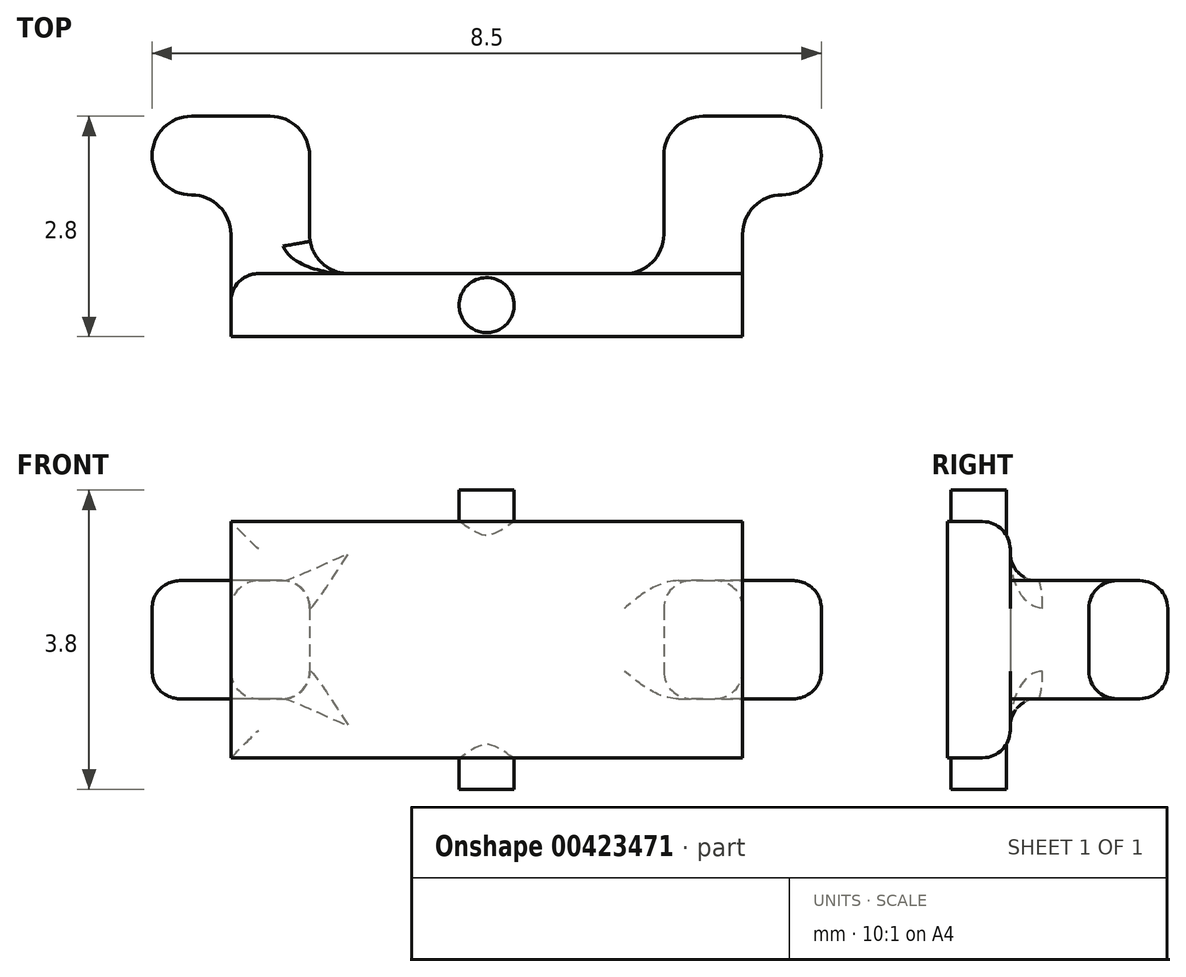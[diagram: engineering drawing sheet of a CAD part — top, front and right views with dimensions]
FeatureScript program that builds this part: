
annotation { "Feature Type Name" : "Feature", "Feature Type Description" : "" }
export const myFeature = defineFeature(function(context is Context, id is Id, definition is map)
    precondition{}
    {
        {
            var Q0;
            Q0=qCreatedBy(makeId("Top.planeOp"),FACE);
            var sketch = newSketch(context, id + "F0", { "sketchPlane" : qUnion([Q0])});
            skLineSegment(sketch, "E0", {"start": v(-3.25, 0) * mm, "end": v(3.25, 0) * mm});
            skPoint(sketch, "E1", {"position": v(0, 0) * mm});
            skLineSegment(sketch, "E2", {"start": v(0, -1.15) * mm, "end": v(0, 7.11) * mm, "construction": true});
            skLineSegment(sketch, "E3", {"start": v(2.25, 1.3) * mm, "end": v(2.25, 2.3) * mm});
            skLineSegment(sketch, "E4", {"start": v(-2.25, 1.3) * mm, "end": v(-2.25, 2.3) * mm});
            skLineSegment(sketch, "E5", {"start": v(-1.75, 0.8) * mm, "end": v(1.75, 0.8) * mm});
            skPoint(sketch, "E6", {"position": v(0, 0.8) * mm});
            skLineSegment(sketch, "E7", {"start": v(-2.75, 2.8) * mm, "end": v(-3.75, 2.8) * mm});
            skLineSegment(sketch, "E8", {"start": v(2.75, 2.8) * mm, "end": v(3.75, 2.8) * mm});
            skLineSegment(sketch, "E9", {"start": v(-4.25, 2.3) * mm, "end": v(-4.25, 2.3) * mm});
            skLineSegment(sketch, "E10", {"start": v(-3.75, 1.8) * mm, "end": v(-3.75, 1.8) * mm});
            skLineSegment(sketch, "E11", {"start": v(-3.25, 1.3) * mm, "end": v(-3.25, 1.3) * mm});
            skLineSegment(sketch, "E12", {"start": v(4.25, 2.3) * mm, "end": v(4.25, 2.3) * mm});
            skLineSegment(sketch, "E13", {"start": v(3.75, 1.8) * mm, "end": v(3.75, 1.8) * mm});
            skLineSegment(sketch, "E14", {"start": v(3.25, 1.3) * mm, "end": v(3.25, 1.3) * mm});
            skPoint(sketch, "E15.visualSharp", {"position": v(-2.25, 0.8) * mm});
            skArc(sketch, "E15.filletArc", {"start": v(-2.25, 1.3) * mm, "mid": v(-2.1, 0.95) * mm, "end": v(-1.75, 0.8) * mm});
            skPoint(sketch, "E16.visualSharp", {"position": v(2.25, 0.8) * mm});
            skArc(sketch, "E16.filletArc", {"start": v(1.75, 0.8) * mm, "mid": v(2.1, 0.95) * mm, "end": v(2.25, 1.3) * mm});
            skPoint(sketch, "E17.visualSharp", {"position": v(3.25, 1.8) * mm});
            skArc(sketch, "E17.filletArc", {"start": v(3.75, 1.8) * mm, "mid": v(3.4, 1.65) * mm, "end": v(3.25, 1.3) * mm});
            skPoint(sketch, "E18.visualSharp", {"position": v(-3.25, 1.8) * mm});
            skArc(sketch, "E18.filletArc", {"start": v(-3.25, 1.3) * mm, "mid": v(-3.4, 1.65) * mm, "end": v(-3.75, 1.8) * mm});
            skPoint(sketch, "E19.visualSharp", {"position": v(-2.25, 2.8) * mm});
            skArc(sketch, "E19.filletArc", {"start": v(-2.25, 2.3) * mm, "mid": v(-2.4, 2.65) * mm, "end": v(-2.75, 2.8) * mm});
            skPoint(sketch, "E20.visualSharp", {"position": v(2.25, 2.8) * mm});
            skArc(sketch, "E20.filletArc", {"start": v(2.75, 2.8) * mm, "mid": v(2.4, 2.65) * mm, "end": v(2.25, 2.3) * mm});
            skPoint(sketch, "E21.visualSharp", {"position": v(4.25, 2.8) * mm});
            skArc(sketch, "E21.filletArc", {"start": v(4.25, 2.3) * mm, "mid": v(4.1, 2.65) * mm, "end": v(3.75, 2.8) * mm});
            skPoint(sketch, "E22.visualSharp", {"position": v(4.25, 1.8) * mm});
            skArc(sketch, "E22.filletArc", {"start": v(3.75, 1.8) * mm, "mid": v(4.1, 1.95) * mm, "end": v(4.25, 2.3) * mm});
            skPoint(sketch, "E23.visualSharp", {"position": v(-4.25, 2.8) * mm});
            skArc(sketch, "E23.filletArc", {"start": v(-3.75, 2.8) * mm, "mid": v(-4.1, 2.65) * mm, "end": v(-4.25, 2.3) * mm});
            skPoint(sketch, "E24.visualSharp", {"position": v(-4.25, 1.8) * mm});
            skArc(sketch, "E24.filletArc", {"start": v(-4.25, 2.3) * mm, "mid": v(-4.1, 1.95) * mm, "end": v(-3.75, 1.8) * mm});
            skLineSegment(sketch, "E25", {"start": v(-3.25, 1.3) * mm, "end": v(-3.25, 0) * mm});
            skLineSegment(sketch, "E26", {"start": v(3.25, 1.3) * mm, "end": v(3.25, 0) * mm});
            skPoint(sketch, "E27.orphan", {"position": v(-5, 0) * mm});
            skPoint(sketch, "E28.orphan", {"position": v(5, 0) * mm});
            skSolve(sketch);
        }
        {
            var Q0;
            Q0=qSketchRegion(id+"F0",true);
            extrude(context, id + "F1", {"entities" : qUnion([Q0]), "depth" : 1.5 * mm, "offsetDistance" : 25 * mm});
        }
        {
            var Q0;
            Q0=makeQuery(id+"F1.opExtrude","CAP_FACE",FACE,{"disambiguationData":[OSD([sQuery(id+"F0.wireOp",EDGE,"E0"),sQuery(id+"F0.wireOp",EDGE,"6YUp3G7D-HScl-yHn5-GseC-h8JY3a3RTnfq"),sQuery(id+"F0.wireOp",EDGE,"Xoj59s7T-2QtX-ZDX5-LiLJ-oQHR1xyVejqm"),sQuery(id+"F0.wireOp",EDGE,"Zc0sCTJD-TUej-OjTx-Aevo-d0EqPVeEhSTX"),sQuery(id+"F0.wireOp",EDGE,"E3"),sQuery(id+"F0.wireOp",EDGE,"E4"),sQuery(id+"F0.wireOp",EDGE,"fb0ed693-0343-43f7-9de8-dc647e30bef6.trimOffspring"),sQuery(id+"F0.wireOp",EDGE,"E5"),sQuery(id+"F0.wireOp",EDGE,"E7"),sQuery(id+"F0.wireOp",EDGE,"E8"),sQuery(id+"F0.wireOp",EDGE,"E15.filletArc"),sQuery(id+"F0.wireOp",EDGE,"E16.filletArc"),sQuery(id+"F0.wireOp",EDGE,"e3a1806a-2c86-475e-80ef-7f3d2f1d7afe.filletArc"),sQuery(id+"F0.wireOp",EDGE,"E17.filletArc"),sQuery(id+"F0.wireOp",EDGE,"63802826-9469-4e69-9e87-4bd683e02e6c.filletArc"),sQuery(id+"F0.wireOp",EDGE,"E18.filletArc"),sQuery(id+"F0.wireOp",EDGE,"E19.filletArc"),sQuery(id+"F0.wireOp",EDGE,"E20.filletArc"),sQuery(id+"F0.wireOp",EDGE,"E21.filletArc"),sQuery(id+"F0.wireOp",EDGE,"E22.filletArc"),sQuery(id+"F0.wireOp",EDGE,"E23.filletArc"),sQuery(id+"F0.wireOp",EDGE,"E24.filletArc")])],"isStart":false});
            var sketch = newSketch(context, id + "F2", { "sketchPlane" : qUnion([Q0])});
            skLineSegment(sketch, "E29.0", {"start": v(-3.25, 0) * mm, "end": v(-3.25, 0) * mm});
            skLineSegment(sketch, "E30.0", {"start": v(-3.25, 0) * mm, "end": v(-3.25, 0.8) * mm});
            skLineSegment(sketch, "E31", {"start": v(-3.25, 0.8) * mm, "end": v(3.25, 0.8) * mm});
            skLineSegment(sketch, "E32.0", {"start": v(-3.25, 0) * mm, "end": v(3.25, 0) * mm});
            skLineSegment(sketch, "E33.0", {"start": v(3.25, 0.8) * mm, "end": v(3.25, 0) * mm});
            skPoint(sketch, "E34.orphan", {"position": v(3.25, 1.3) * mm});
            skSolve(sketch);
        }
        {
            var Q0;
            Q0=qSketchRegion(id+"F2",true);
            extrude(context, id + "F3", {"entities" : qUnion([Q0]), "operationType" : NewBodyOperationType.ADD, "depth" : 0.75 * mm, "offsetDistance" : 25 * mm});
        }
        {
            var Q0;
            Q0=makeQuery(id+"F1.opExtrude","CAP_FACE",FACE,{"disambiguationData":[OSD([sQuery(id+"F0.wireOp",EDGE,"E0"),sQuery(id+"F0.wireOp",EDGE,"E3"),sQuery(id+"F0.wireOp",EDGE,"E4"),sQuery(id+"F0.wireOp",EDGE,"E5"),sQuery(id+"F0.wireOp",EDGE,"E7"),sQuery(id+"F0.wireOp",EDGE,"E8"),sQuery(id+"F0.wireOp",EDGE,"E15.filletArc"),sQuery(id+"F0.wireOp",EDGE,"E16.filletArc"),sQuery(id+"F0.wireOp",EDGE,"E17.filletArc"),sQuery(id+"F0.wireOp",EDGE,"E18.filletArc"),sQuery(id+"F0.wireOp",EDGE,"E19.filletArc"),sQuery(id+"F0.wireOp",EDGE,"E20.filletArc"),sQuery(id+"F0.wireOp",EDGE,"E21.filletArc"),sQuery(id+"F0.wireOp",EDGE,"E22.filletArc"),sQuery(id+"F0.wireOp",EDGE,"E23.filletArc"),sQuery(id+"F0.wireOp",EDGE,"E24.filletArc"),sQuery(id+"F0.wireOp",EDGE,"E25"),sQuery(id+"F0.wireOp",EDGE,"E26")])],"isStart":true});
            var sketch = newSketch(context, id + "F4", { "sketchPlane" : qUnion([Q0])});
            skLineSegment(sketch, "E35.0", {"start": v(-3.25, -0.8) * mm, "end": v(3.25, -0.8) * mm});
            skLineSegment(sketch, "E36.0", {"start": v(3.25, -0.8) * mm, "end": v(3.25, 0) * mm});
            skLineSegment(sketch, "E37.0", {"start": v(-3.25, 0) * mm, "end": v(3.25, 0) * mm});
            skLineSegment(sketch, "E38.0", {"start": v(-3.25, 0) * mm, "end": v(-3.25, -0.8) * mm});
            skSolve(sketch);
        }
        {
            var Q0;
            Q0=qSketchRegion(id+"F4",true);
            extrude(context, id + "F5", {"entities" : qUnion([Q0]), "operationType" : NewBodyOperationType.ADD, "depth" : 0.75 * mm, "offsetDistance" : 25 * mm});
        }
        {
            var Q0;
            {var subQ5=sQuery(id+"F0.wireOp",EDGE,"E15.filletArc");var subQ6=sQuery(id+"F2.wireOp",EDGE,"E31");Q0=makeQuery(id+"F3.boolean.opBoolean","SPLIT",EDGE,{"disambiguationData":[TD([makeQuery(id+"F1.opExtrude","SWEPT_FACE",FACE,{"disambiguationData":[OSD([subQ5])]})])],"derivedFrom":makeQuery(id+"F3.opExtrude","CAP_EDGE",EDGE,{"disambiguationData":[OSD([subQ6])],"isStart":true})});}
            var Q1;
            {var subQ5=sQuery(id+"F0.wireOp",EDGE,"E16.filletArc");var subQ6=sQuery(id+"F2.wireOp",EDGE,"E31");Q1=makeQuery(id+"F3.boolean.opBoolean","SPLIT",EDGE,{"disambiguationData":[TD([makeQuery(id+"F1.opExtrude","SWEPT_FACE",FACE,{"disambiguationData":[OSD([subQ5])]})])],"derivedFrom":makeQuery(id+"F3.opExtrude","CAP_EDGE",EDGE,{"disambiguationData":[OSD([subQ6])],"isStart":true})});}
            var Q2;
            {var subQ0=sQuery(id+"F0.wireOp",EDGE,"E15.filletArc");var subQ3=sQuery(id+"F4.wireOp",EDGE,"E35.0");Q2=makeQuery(id+"F5.boolean.opBoolean","SPLIT",EDGE,{"disambiguationData":[TD([makeQuery(id+"F1.opExtrude","SWEPT_FACE",FACE,{"disambiguationData":[OSD([subQ0])]})])],"derivedFrom":makeQuery(id+"F5.opExtrude","CAP_EDGE",EDGE,{"disambiguationData":[OSD([subQ3])],"isStart":true})});}
            var Q3;
            {var subQ1=sQuery(id+"F4.wireOp",EDGE,"E35.0");var subQ2=sQuery(id+"F0.wireOp",EDGE,"E16.filletArc");Q3=makeQuery(id+"F5.boolean.opBoolean","SPLIT",EDGE,{"disambiguationData":[TD([makeQuery(id+"F1.opExtrude","SWEPT_FACE",FACE,{"disambiguationData":[OSD([subQ2])]})])],"derivedFrom":makeQuery(id+"F5.opExtrude","CAP_EDGE",EDGE,{"disambiguationData":[OSD([subQ1])],"isStart":true})});}
            fillet(context, id + "F6", {"entities" : qUnion([Q0, Q1, Q2, Q3]), "radius" : 0.35 * mm, "tangentPropagation" : true, "defaultsChanged" : true, "vertexSettings" : [], "allowEdgeOverflow" : false});
        }
        {
            var Q0;
            Q0=makeQuery(id+"F5.opExtrude","CAP_EDGE",EDGE,{"disambiguationData":[OSD([sQuery(id+"F4.wireOp",EDGE,"E35.0")])],"isStart":false});
            var Q1;
            Q1=makeQuery(id+"F3.opExtrude","CAP_EDGE",EDGE,{"disambiguationData":[OSD([sQuery(id+"F2.wireOp",EDGE,"E31")])],"isStart":false});
            var Q2;
            Q2=makeQuery(id+"F1.opExtrude","CAP_EDGE",EDGE,{"disambiguationData":[OSD([sQuery(id+"F0.wireOp",EDGE,"E7")])],"isStart":true});
            var Q3;
            Q3=makeQuery(id+"F1.opExtrude","CAP_EDGE",EDGE,{"disambiguationData":[OSD([sQuery(id+"F0.wireOp",EDGE,"E8")])],"isStart":true});
            var Q4;
            Q4=makeQuery(id+"F1.opExtrude","CAP_EDGE",EDGE,{"disambiguationData":[OSD([sQuery(id+"F0.wireOp",EDGE,"E8")])],"isStart":false});
            var Q5;
            Q5=makeQuery(id+"F1.opExtrude","CAP_EDGE",EDGE,{"disambiguationData":[OSD([sQuery(id+"F0.wireOp",EDGE,"E7")])],"isStart":false});
            fillet(context, id + "F7", {"entities" : qUnion([Q0, Q1, Q2, Q3, Q4, Q5]), "tangentPropagation" : true, "radius" : 0.35 * mm, "defaultsChanged" : false, "vertexSettings" : [], "allowEdgeOverflow" : false});
        }
        {
            var Q0;
            Q0=makeQuery(id+"F3.opExtrude","CAP_FACE",FACE,{"disambiguationData":[OSD([sQuery(id+"F2.wireOp",EDGE,"E30.0"),sQuery(id+"F2.wireOp",EDGE,"E31"),sQuery(id+"F2.wireOp",EDGE,"E32.0"),sQuery(id+"F2.wireOp",EDGE,"E33.0")])],"isStart":false});
            var sketch = newSketch(context, id + "F8", { "sketchPlane" : qUnion([Q0])});
            skLineSegment(sketch, "E39.0", {"start": v(-3.25, 0) * mm, "end": v(3.25, 0) * mm, "construction": true});
            skLineSegment(sketch, "E40.0", {"start": v(-2.9, 0.8) * mm, "end": v(2.9, 0.8) * mm, "construction": true});
            skPoint(sketch, "E41", {"position": v(0, 0.8) * mm});
            skPoint(sketch, "E42", {"position": v(0, 0) * mm});
            skLineSegment(sketch, "E43", {"start": v(0, 0.8) * mm, "end": v(0, 0) * mm, "construction": true});
            skPoint(sketch, "E44", {"position": v(0, 0.4) * mm});
            skCircle(sketch, "E45", {"center": v(0, 0.4) * mm, "radius": 0.35 * mm});
            skSolve(sketch);
        }
        {
            var Q0;
            Q0=qSketchRegion(id+"F8",true);
            extrude(context, id + "F9", {"entities" : qUnion([Q0]), "operationType" : NewBodyOperationType.ADD, "depth" : 0.4 * mm, "offsetDistance" : 25 * mm, "hasSecondDirection" : true, "secondDirectionOppositeDirection" : true, "secondDirectionDepth" : 3.4 * mm});
        }
    });
